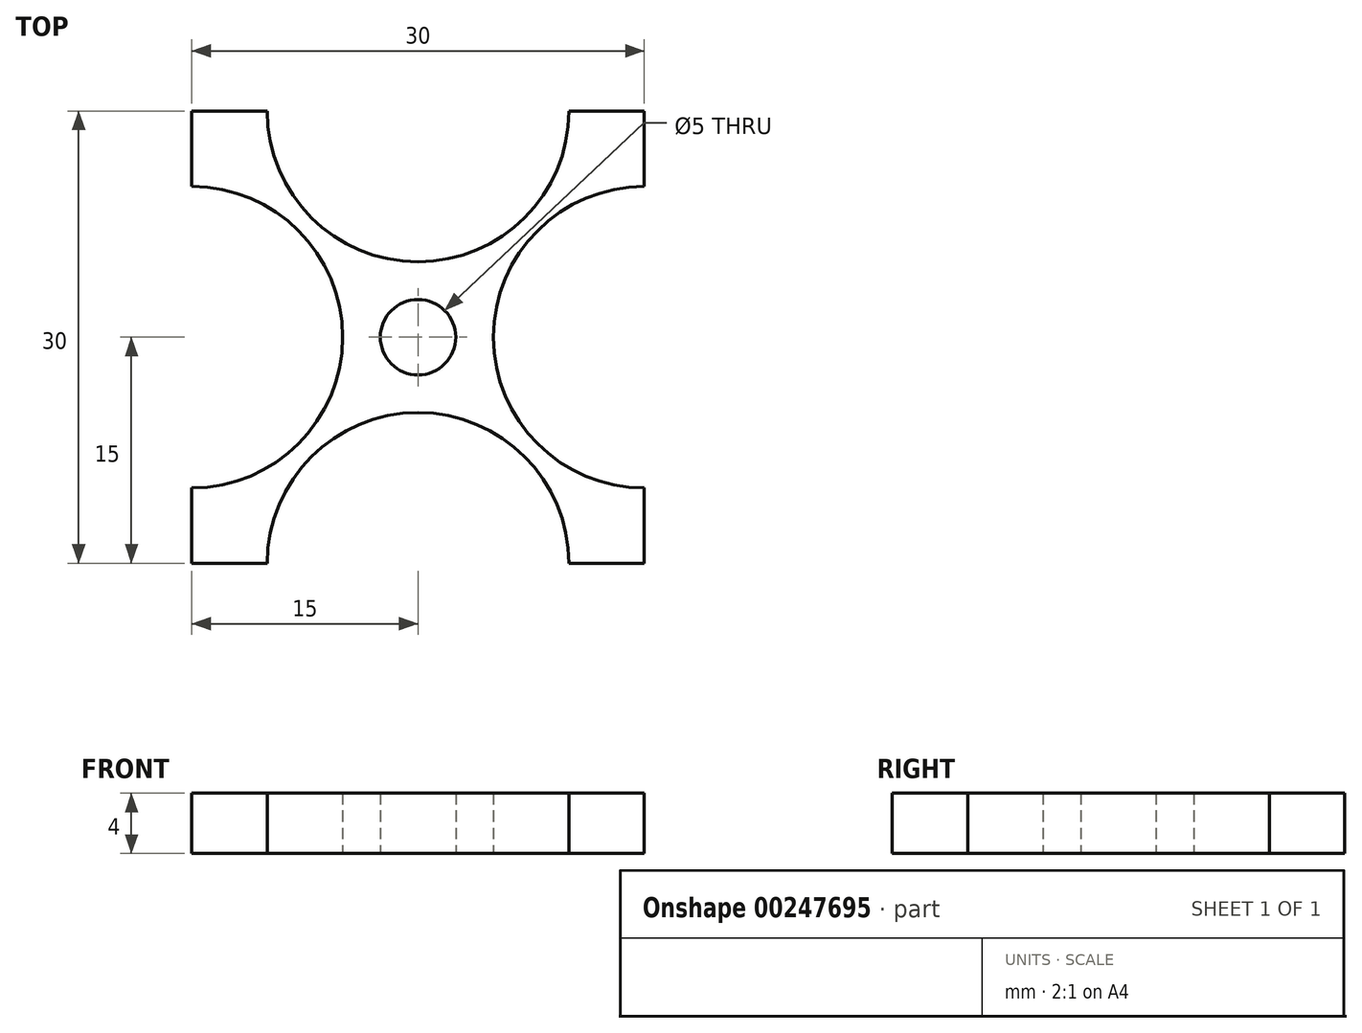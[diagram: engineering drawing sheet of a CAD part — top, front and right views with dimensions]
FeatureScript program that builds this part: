
annotation { "Feature Type Name" : "Feature", "Feature Type Description" : "" }
export const myFeature = defineFeature(function(context is Context, id is Id, definition is map)
    precondition{}
    {
        {
            var Q0;
            Q0=qCreatedBy(makeId("Top.planeOp"),FACE);
            var sketch = newSketch(context, id + "F0", { "sketchPlane" : qUnion([Q0])});
            skLineSegment(sketch, "E0.bottom", {"start": v(15, 15) * mm, "end": v(-15, 15) * mm});
            skLineSegment(sketch, "E0.top", {"start": v(15, -15) * mm, "end": v(-15, -15) * mm});
            skLineSegment(sketch, "E0.left", {"start": v(15, 15) * mm, "end": v(15, -15) * mm});
            skLineSegment(sketch, "E0.right", {"start": v(-15, 15) * mm, "end": v(-15, -15) * mm});
            skPoint(sketch, "E0.middle", {"position": v(0, 0) * mm});
            skCircle(sketch, "E1", {"center": v(0, 15) * mm, "radius": 10 * mm});
            skCircle(sketch, "E2", {"center": v(0, -15) * mm, "radius": 10 * mm});
            skCircle(sketch, "E3", {"center": v(-15, 0) * mm, "radius": 10 * mm});
            skCircle(sketch, "E4", {"center": v(15, 0) * mm, "radius": 10 * mm});
            skCircle(sketch, "E5", {"center": v(0, 0) * mm, "radius": 2.5 * mm});
            skSolve(sketch);
        }
        {
            var Q0;
            Q0=makeQuery(id+"F0.imprint","IMPRINT",FACE,{"disambiguationData":[TD([[makeQuery(id+"F0.imprint","IMPRINT",EDGE,{"derivedFrom":sQuery(id+"F0.wireOp",EDGE,"E5")}),-1.0]])]});
            extrude(context, id + "F1", {"entities" : qUnion([Q0]), "depth" : 4 * mm});
        }
    });
